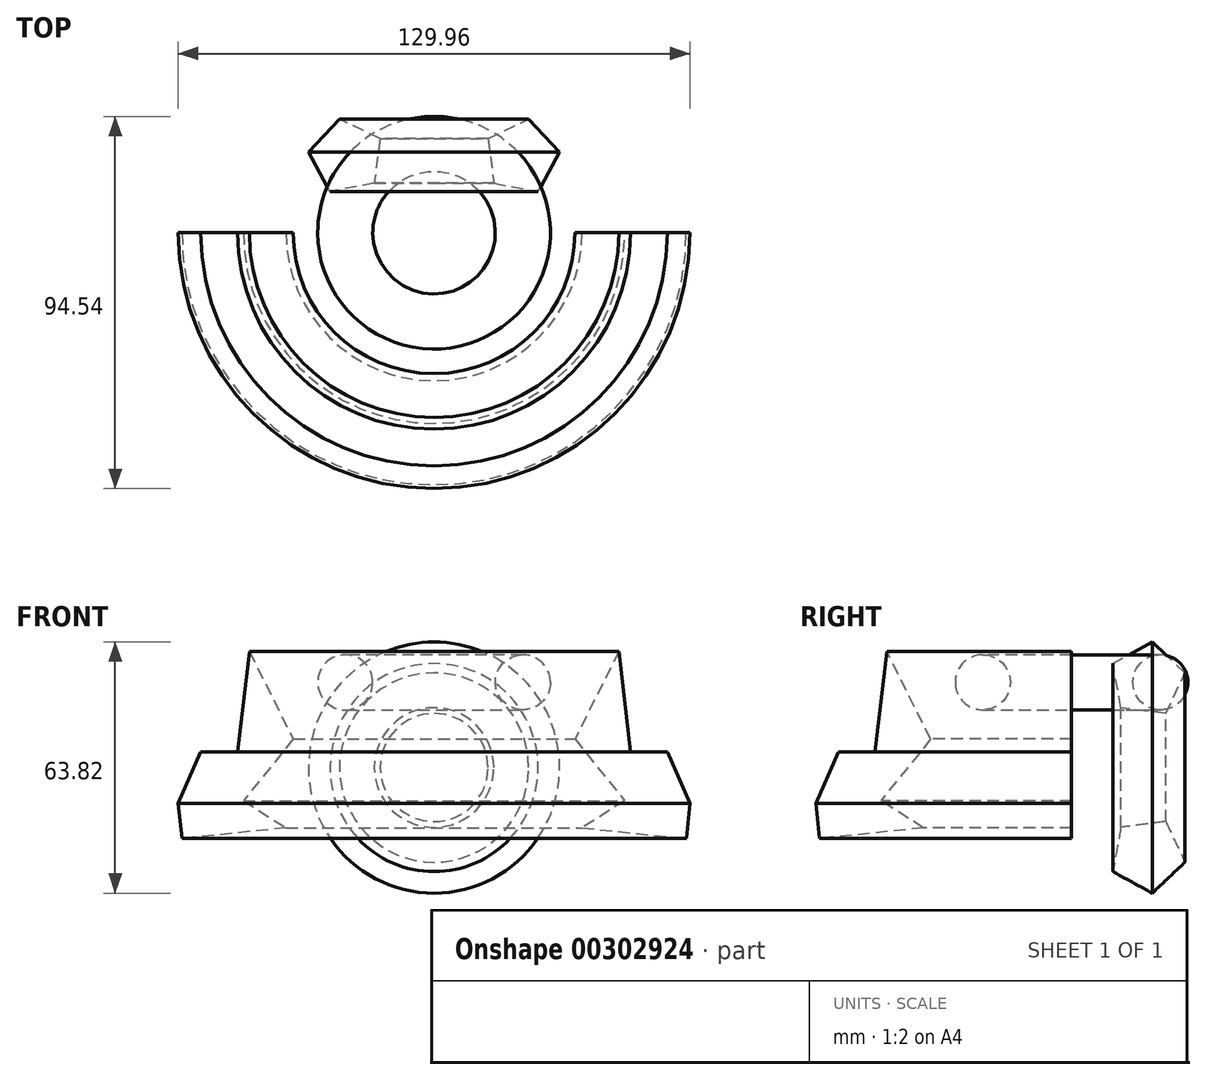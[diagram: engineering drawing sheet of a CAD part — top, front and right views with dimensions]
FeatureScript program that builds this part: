
annotation { "Feature Type Name" : "Feature", "Feature Type Description" : "" }
export const myFeature = defineFeature(function(context is Context, id is Id, definition is map)
    precondition{}
    {
        {
            var Q0;
            Q0=qCreatedBy(makeId("Right.planeOp"),FACE);
            var sketch = newSketch(context, id + "F0", { "sketchPlane" : qUnion([Q0])});
            skLineSegment(sketch, "E0", {"start": v(0, 0) * mm, "end": v(0, 37.9) * mm});
            skCircle(sketch, "E1", {"center": v(22.56, 21.66) * mm, "radius": 7 * mm});
            skSolve(sketch);
        }
        {
            var Q0;
            Q0=makeQuery(id+"F0.imprint","IMPRINT",FACE,{"disambiguationData":[TD([[makeQuery(id+"F0.imprint","IMPRINT",EDGE,{"derivedFrom":sQuery(id+"F0.wireOp",EDGE,"E1")}),1.0]])]});
            var Q1;
            Q1=sQuery(id+"F0.wireOp",EDGE,"E0");
            revolve(context, id + "F1", {"entities" : qUnion([Q0]), "axis" : qUnion([Q1]), "revolveType" : RevolveType.FULL});
        }
        {
            var Q0;
            Q0=qCreatedBy(makeId("Right.planeOp"),FACE);
            var sketch = newSketch(context, id + "F2", { "sketchPlane" : qUnion([Q0])});
            skCircle(sketch, "E2.cCircle", {"center": v(19.25, -22.26) * mm, "radius": 7.87 * mm, "construction": true});
            skLineSegment(sketch, "E2.0", {"start": v(28.82, -24.04) * mm, "end": v(20.51, -31.9) * mm});
            skLineSegment(sketch, "E2.1", {"start": v(20.51, -31.9) * mm, "end": v(10.46, -26.44) * mm});
            skLineSegment(sketch, "E2.2", {"start": v(10.46, -26.44) * mm, "end": v(12.56, -15.2) * mm});
            skLineSegment(sketch, "E2.3", {"start": v(12.56, -15.2) * mm, "end": v(23.9, -13.71) * mm});
            skLineSegment(sketch, "E2.4", {"start": v(23.9, -13.71) * mm, "end": v(28.82, -24.04) * mm});
            skPoint(sketch, "E2.0.midPoint", {"position": v(24.66, -27.97) * mm});
            skLineSegment(sketch, "E3", {"start": v(0, 0) * mm, "end": v(0, -35.2) * mm});
            skLineSegment(sketch, "E4", {"start": v(0, 0) * mm, "end": v(37.9, 0) * mm});
            skSolve(sketch);
        }
        {
            var Q0;
            Q0=makeQuery(id+"F2.imprint","IMPRINT",FACE,{"disambiguationData":[TD([[makeQuery(id+"F2.imprint","IMPRINT",EDGE,{"derivedFrom":sQuery(id+"F2.wireOp",EDGE,"E2.0")}),-1.0]])]});
            var Q1;
            Q1=sQuery(id+"F2.wireOp",EDGE,"E4");
            revolve(context, id + "F3", {"entities" : qUnion([Q0]), "axis" : qUnion([Q1]), "revolveType" : RevolveType.FULL});
        }
        {
            var Q0;
            Q0=qCreatedBy(makeId("Right.planeOp"),FACE);
            var sketch = newSketch(context, id + "F4", { "sketchPlane" : qUnion([Q0])});
            skLineSegment(sketch, "E5", {"start": v(-48.43, -8.42) * mm, "end": v(-37.6, -15.34) * mm});
            skLineSegment(sketch, "E6", {"start": v(-37.6, -15.34) * mm, "end": v(-64.07, -18.05) * mm});
            skLineSegment(sketch, "E7", {"start": v(-64.07, -18.05) * mm, "end": v(-64.98, -9.12) * mm});
            skLineSegment(sketch, "E8", {"start": v(-64.98, -9.12) * mm, "end": v(-59.26, 3.91) * mm});
            skLineSegment(sketch, "E9", {"start": v(-59.26, 3.91) * mm, "end": v(-49.93, 3.91) * mm});
            skLineSegment(sketch, "E10", {"start": v(-49.93, 3.91) * mm, "end": v(-46.92, 29.48) * mm});
            skLineSegment(sketch, "E11", {"start": v(-46.92, 29.48) * mm, "end": v(-35.8, 7.22) * mm});
            skLineSegment(sketch, "E12", {"start": v(-35.8, 7.22) * mm, "end": v(-48.43, -8.42) * mm});
            skLineSegment(sketch, "E13", {"start": v(0, 0) * mm, "end": v(0, -13.38) * mm});
            skSolve(sketch);
        }
        {
            var Q0;
            Q0=makeQuery(id+"F4.imprint","IMPRINT",FACE,{"disambiguationData":[TD([[makeQuery(id+"F4.imprint","IMPRINT",EDGE,{"derivedFrom":sQuery(id+"F4.wireOp",EDGE,"E5")}),-1.0]])]});
            var Q1;
            Q1=sQuery(id+"F4.wireOp",EDGE,"E13");
            revolve(context, id + "F5", {"entities" : qUnion([Q0]), "axis" : qUnion([Q1]), "revolveType" : RevolveType.SYMMETRIC, "angle" : 180 * degree});
        }
    });
